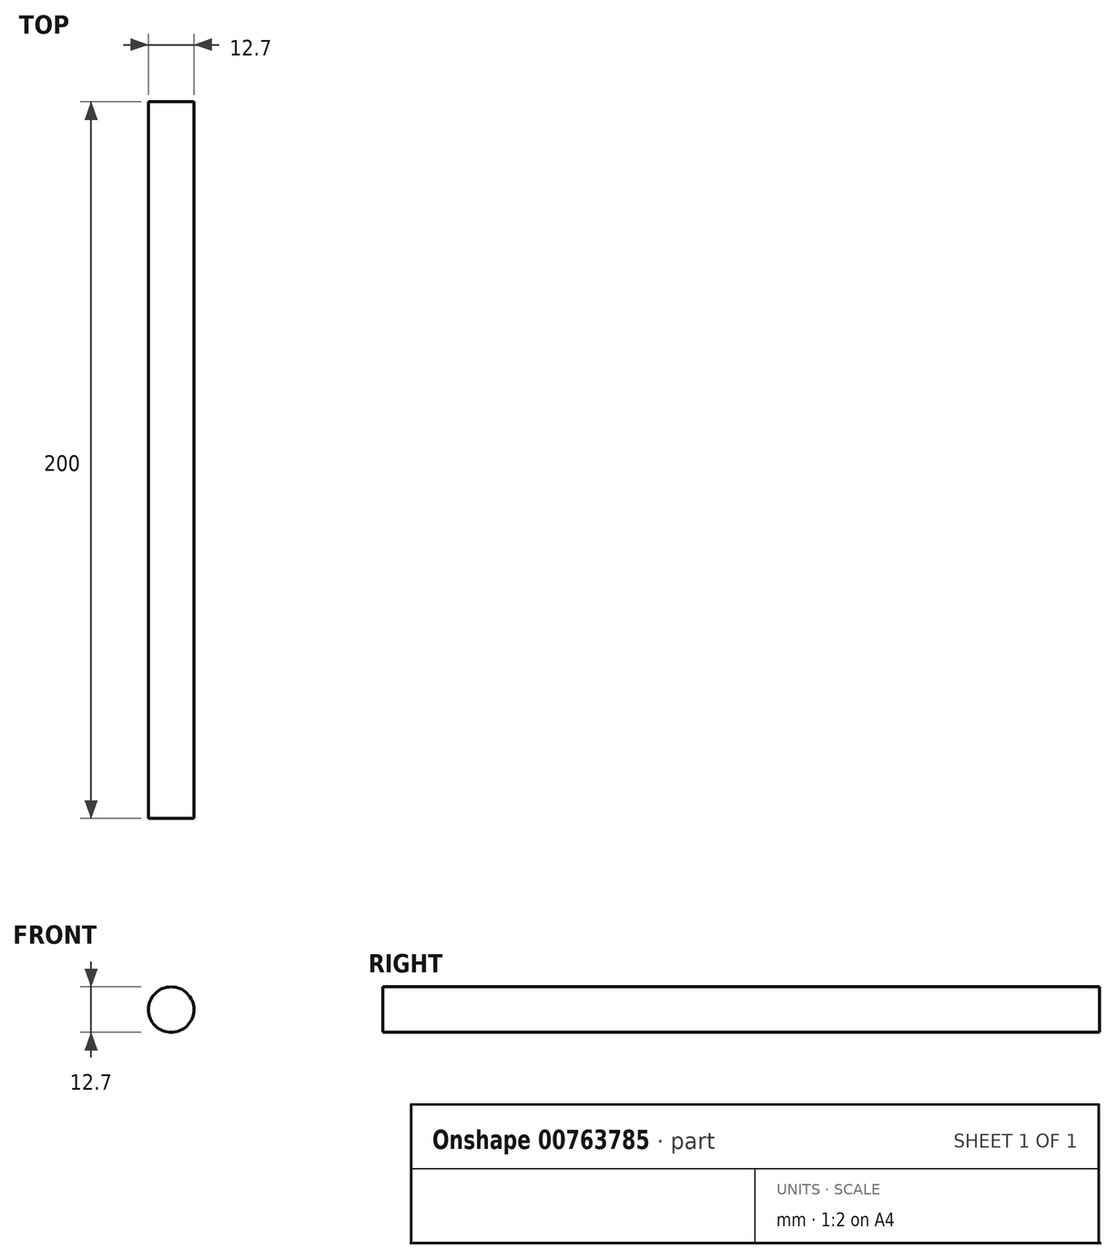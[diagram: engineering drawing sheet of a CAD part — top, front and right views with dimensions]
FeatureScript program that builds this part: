
annotation { "Feature Type Name" : "Feature", "Feature Type Description" : "" }
export const myFeature = defineFeature(function(context is Context, id is Id, definition is map)
    precondition{}
    {
        {
            var Q0;
            Q0=qCreatedBy(makeId("Front.planeOp"),FACE);
            var sketch = newSketch(context, id + "F0", { "sketchPlane" : qUnion([Q0])});
            skCircle(sketch, "E0", {"center": v(0, 0) * mm, "radius": 6.35 * mm});
            skSolve(sketch);
        }
        {
            var Q0;
            Q0=makeQuery(id+"F0.imprint","IMPRINT",FACE,{"disambiguationData":[TD([[makeQuery(id+"F0.imprint","IMPRINT",EDGE,{"derivedFrom":sQuery(id+"F0.wireOp",EDGE,"E0")}),1.0]])]});
            extrude(context, id + "F1", {"entities" : qUnion([Q0]), "oppositeDirection" : true, "depth" : 200 * mm, "offsetDistance" : 25 * mm});
        }
    });
